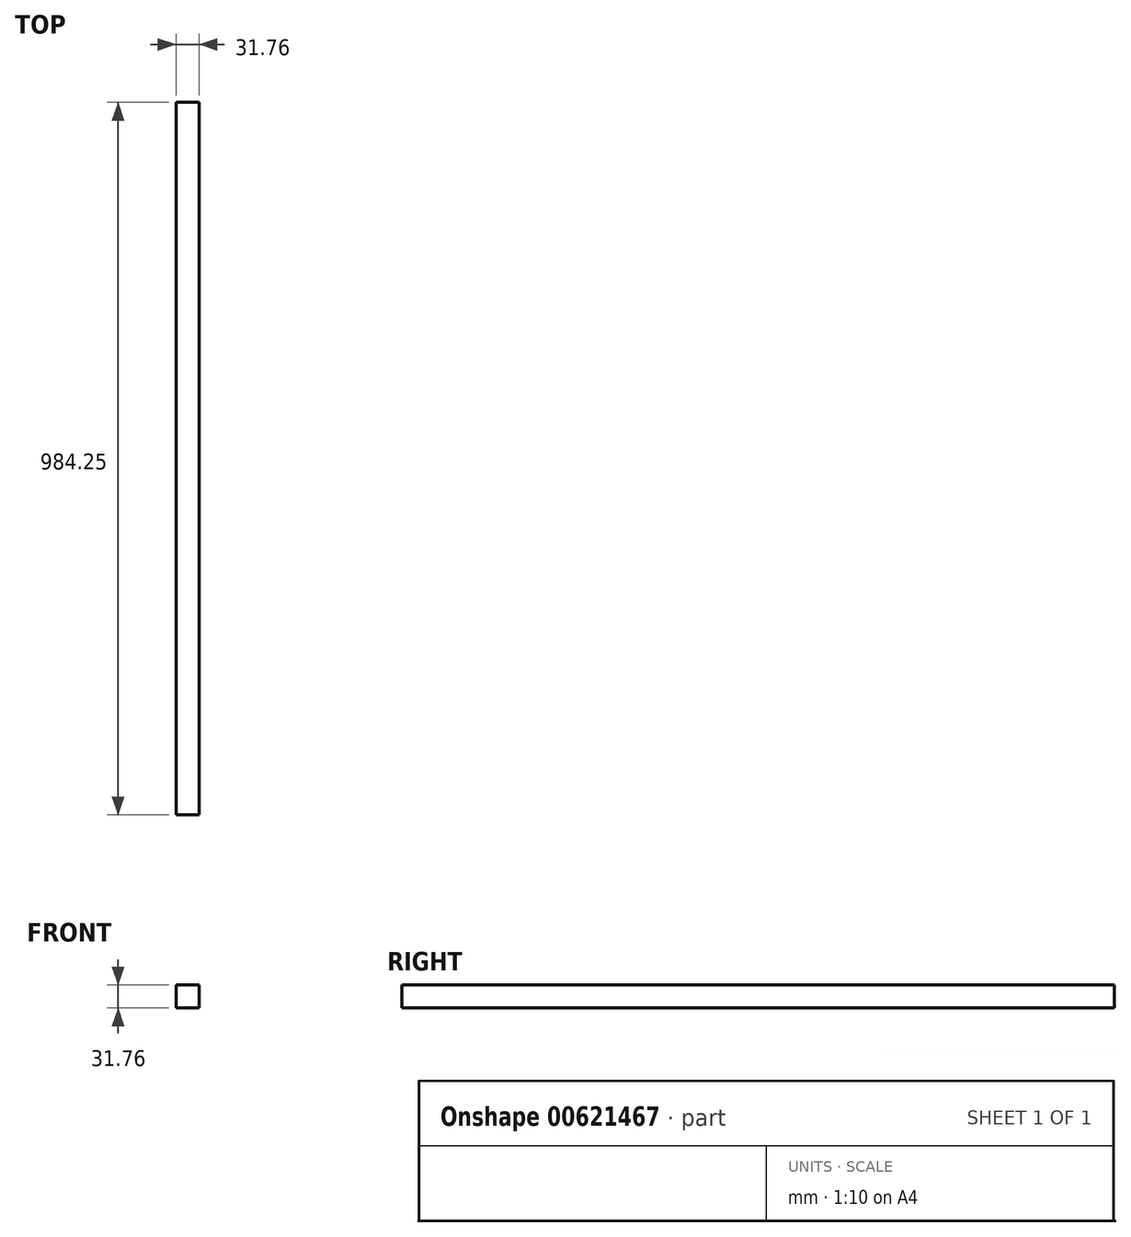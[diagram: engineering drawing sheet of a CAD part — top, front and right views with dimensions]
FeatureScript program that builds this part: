
annotation { "Feature Type Name" : "Feature", "Feature Type Description" : "" }
export const myFeature = defineFeature(function(context is Context, id is Id, definition is map)
    precondition{}
    {
        {
            var Q0;
            Q0=qCreatedBy(makeId("Front.planeOp"),FACE);
            var sketch = newSketch(context, id + "F0", { "sketchPlane" : qUnion([Q0])});
            skLineSegment(sketch, "E0.bottom", {"start": v(15.88, 15.88) * mm, "end": v(-15.88, 15.88) * mm});
            skLineSegment(sketch, "E0.top", {"start": v(15.88, -15.88) * mm, "end": v(-15.88, -15.88) * mm});
            skLineSegment(sketch, "E0.left", {"start": v(15.88, 15.87) * mm, "end": v(15.88, -15.88) * mm});
            skLineSegment(sketch, "E0.right", {"start": v(-15.88, 15.88) * mm, "end": v(-15.88, -15.88) * mm});
            skPoint(sketch, "E0.middle", {"position": v(0, 0) * mm});
            skSolve(sketch);
        }
        {
            var Q0;
            Q0 = qSketchRegion(id + "F0", true);
            extrude(context, id + "F1", {"entities" : qUnion([Q0]), "depth" : 984.25 * mm, "offsetDistance" : 25.4 * mm});
        }
    });
